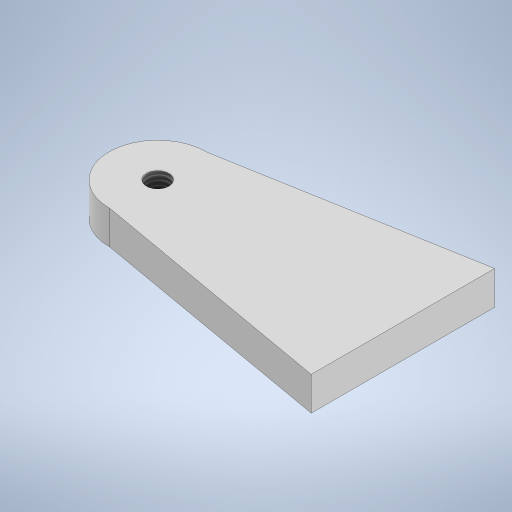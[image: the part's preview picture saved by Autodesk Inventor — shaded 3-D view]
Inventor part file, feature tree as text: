
AUTODESK INVENTOR PART (.ipt)
format: ipt  version: 2023 (Build 270158000, 158)  size: 221,184 bytes
history: native  units: mm
features: sketch x1, extrude x1, hole x1
ambient origin geometry x8: Origin, YZ Plane, XZ Plane, XY Plane, X Axis, Y Axis, Z Axis, Center Point
bodies: Solid1 (feature_tree)
feature tree (3):
  sketch  "Sketch1"  dims[d0=30.0mm d1=13.962634mm d4=13.962634mm d7=15.896035mm d9=40.128778mm d10=7.803844mm d11=5.5mm d12=0.0mm d13=3.688101mm d14=9.0mm d15=4.0mm d16=2.0mm d17=90.0deg d18=13.0mm d19=20.594885mm]
  extrude  "Extrusion1"  Depth=5.5mm
  hole  "Hole1"  [1 undecoded]
note: 1 required parameter value undecoded (feature->parameter linkage not recoverable at this tier; creation-order binding heuristic only, values carry confidence <= 0.55)
